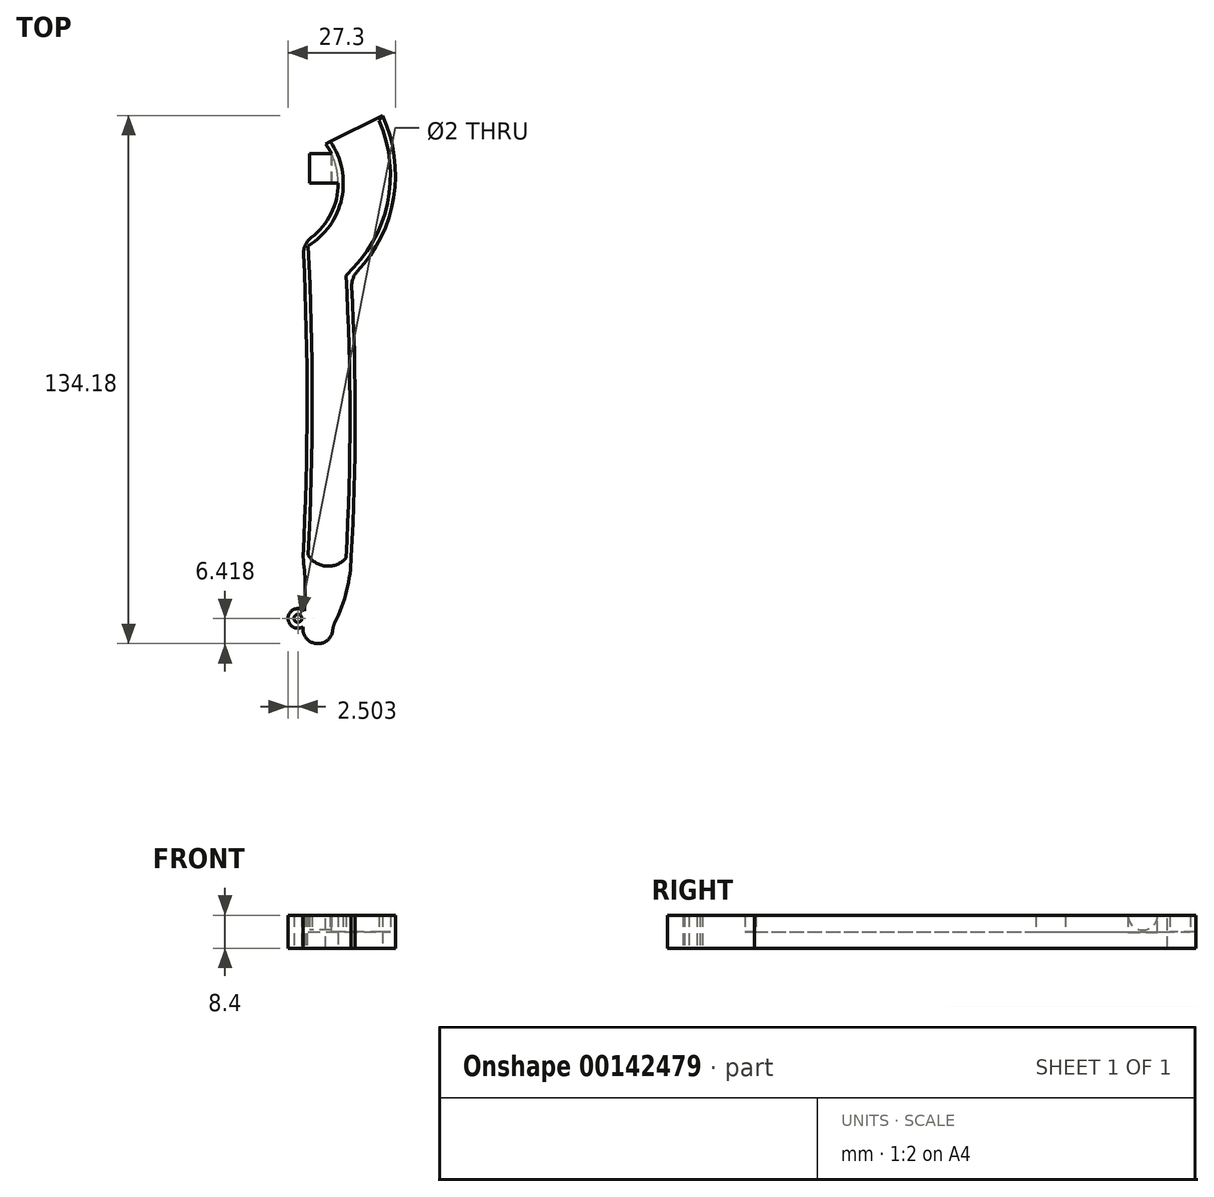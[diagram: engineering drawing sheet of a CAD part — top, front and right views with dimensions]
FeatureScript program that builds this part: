
annotation { "Feature Type Name" : "Feature", "Feature Type Description" : "" }
export const myFeature = defineFeature(function(context is Context, id is Id, definition is map)
    precondition{}
    {
        {
            var Q0;
            Q0=qCreatedBy(makeId("Top.planeOp"),FACE);
            var sketch = newSketch(context, id + "F0", { "sketchPlane" : qUnion([Q0])});
            skArc(sketch, "E0", {"start": v(-18, -31.8) * mm, "mid": v(-9.08, -15.9) * mm, "end": v(-18, 0) * mm});
            skArc(sketch, "E1", {"start": v(-8.38, -39.3) * mm, "mid": v(2.12, -21) * mm, "end": v(0, 0) * mm});
            skArc(sketch, "E2", {"start": v(-18, -110.4) * mm, "mid": v(-17, -71.1) * mm, "end": v(-18, -31.8) * mm});
            skArc(sketch, "E3", {"start": v(-8.38, -111.1) * mm, "mid": v(-7.37, -75.2) * mm, "end": v(-8.38, -39.3) * mm});
            skArc(sketch, "E4", {"start": v(-18, -110.4) * mm, "mid": v(-13.37, -113.18) * mm, "end": v(-8.38, -111.1) * mm});
            skLineSegment(sketch, "E5", {"start": v(0, 0) * mm, "end": v(-18, 0) * mm});
            skArc(sketch, "E6.0", {"start": v(-19.32, -110.8) * mm, "mid": v(-18.3, -70.94) * mm, "end": v(-19.34, -31.07) * mm});
            skLineSegment(sketch, "E6.1", {"start": v(0.84, 1.3) * mm, "end": v(-25.59, 1.3) * mm});
            skArc(sketch, "E6.2", {"start": v(-7.05, -39.84) * mm, "mid": v(3.54, -20.54) * mm, "end": v(0.84, 1.3) * mm});
            skArc(sketch, "E6.3", {"start": v(-19.34, -31.07) * mm, "mid": v(-10.7, -12.62) * mm, "end": v(-25.59, 1.3) * mm});
            skArc(sketch, "E6.4", {"start": v(-7.06, -110.8) * mm, "mid": v(-6.07, -75.32) * mm, "end": v(-7.05, -39.84) * mm});
            skArc(sketch, "E7", {"start": v(-19.32, -128.6) * mm, "mid": v(-18.75, -119.7) * mm, "end": v(-19.32, -110.8) * mm});
            skArc(sketch, "E8", {"start": v(-11.78, -128.6) * mm, "mid": v(-8.38, -119.98) * mm, "end": v(-7.06, -110.8) * mm});
            skArc(sketch, "E9", {"start": v(-19.32, -128.6) * mm, "mid": v(-15.55, -132.88) * mm, "end": v(-11.78, -128.6) * mm});
            skArc(sketch, "E10", {"start": v(-18.93, -124.62) * mm, "mid": v(-23.1, -126.21) * mm, "end": v(-19.32, -128.6) * mm});
            skCircle(sketch, "E11", {"center": v(-20.62, -126.46) * mm, "radius": 1 * mm});
            skLineSegment(sketch, "E12", {"start": v(-10.38, -15.9) * mm, "end": v(-17.68, -15.9) * mm});
            skLineSegment(sketch, "E13", {"start": v(-17.68, -15.9) * mm, "end": v(-17.68, -8.4) * mm});
            skLineSegment(sketch, "E14", {"start": v(-17.68, -8.4) * mm, "end": v(-12.09, -8.4) * mm});
            skSolve(sketch);
        }
        {
            var Q0;
            Q0=makeQuery(id+"F0.imprint","IMPRINT",FACE,{"disambiguationData":[TD([[makeQuery(id+"F0.imprint","IMPRINT",EDGE,{"derivedFrom":sQuery(id+"F0.wireOp",EDGE,"E0")}),1.0]])]});
            var Q1;
            {var subQ0=sQuery(id+"F0.wireOp",EDGE,"E10");Q1=makeQuery(id+"F0.imprint","IMPRINT",FACE,{"disambiguationData":[TD([[makeQuery(id+"F0.imprint","IMPRINT",EDGE,{"derivedFrom":subQ0}),1.0]])]});}
            extrude(context, id + "F1", {"entities" : qUnion([Q0, Q1]), "depth" : 8.4 * mm});
        }
        {
            var Q0;
            Q0=makeQuery(id+"F0.imprint","IMPRINT",FACE,{"disambiguationData":[TD([[makeQuery(id+"F0.imprint","IMPRINT",EDGE,{"derivedFrom":sQuery(id+"F0.wireOp",EDGE,"E0")}),-1.0]])]});
            extrude(context, id + "F2", {"entities" : qUnion([Q0]), "operationType" : NewBodyOperationType.ADD, "depth" : 4.2 * mm});
        }
        {
            var Q0;
            {var subQ0=sQuery(id+"F0.wireOp",EDGE,"E12");Q0=makeQuery(id+"F0.imprint","IMPRINT",FACE,{"disambiguationData":[TD([[makeQuery(id+"F0.imprint","IMPRINT",EDGE,{"derivedFrom":subQ0}),-1.0]])]});}
            extrude(context, id + "F3", {"entities" : qUnion([Q0]), "operationType" : NewBodyOperationType.ADD, "depth" : 8.4 * mm});
        }
        {
            var Q0;
            {var subQ0=sQuery(id+"F0.wireOp",EDGE,"E12");Q0=makeQuery(id+"F0.imprint","IMPRINT",FACE,{"disambiguationData":[TD([[makeQuery(id+"F0.imprint","IMPRINT",EDGE,{"derivedFrom":subQ0}),-1.0]])]});}
            extrude(context, id + "F4", {"entities" : qUnion([Q0]), "operationType" : NewBodyOperationType.REMOVE, "depth" : 4 * mm});
        }
        {
            var Q0;
            Q0=makeQuery(id+"F3.opExtrude","SWEPT_FACE",FACE,{"disambiguationData":[OSD([sQuery(id+"F0.wireOp",EDGE,"E13")])]});
            var sketch = newSketch(context, id + "F5", { "sketchPlane" : qUnion([Q0])});
            skLineSegment(sketch, "E15.0", {"start": v(8.4, 8.4) * mm, "end": v(8.4, 4) * mm});
            skLineSegment(sketch, "E15.1", {"start": v(15.9, 8.4) * mm, "end": v(8.4, 8.4) * mm});
            skLineSegment(sketch, "E15.2", {"start": v(15.9, 8.4) * mm, "end": v(15.9, 4) * mm});
            skLineSegment(sketch, "E15.3", {"start": v(15.9, 4) * mm, "end": v(8.4, 4) * mm});
            skSolve(sketch);
        }
        {
            var Q0;
            {var subQ0=sQuery(id+"F0.wireOp",EDGE,"E6.3");Q0=makeQuery(id+"F3.boolean.opBoolean","MERGE",FACE,{"derivedFrom":[makeQuery(id+"F1.opExtrude","CAP_FACE",FACE,{"disambiguationData":[OSD([sQuery(id+"F0.wireOp",EDGE,"E0"),sQuery(id+"F0.wireOp",EDGE,"E1"),sQuery(id+"F0.wireOp",EDGE,"E2"),sQuery(id+"F0.wireOp",EDGE,"E3"),sQuery(id+"F0.wireOp",EDGE,"E4"),sQuery(id+"F0.wireOp",EDGE,"E5"),sQuery(id+"F0.wireOp",EDGE,"E6.0"),sQuery(id+"F0.wireOp",EDGE,"E6.1"),sQuery(id+"F0.wireOp",EDGE,"E6.2"),subQ0,sQuery(id+"F0.wireOp",EDGE,"E6.4"),sQuery(id+"F0.wireOp",EDGE,"E7"),sQuery(id+"F0.wireOp",EDGE,"E8"),sQuery(id+"F0.wireOp",EDGE,"E9"),sQuery(id+"F0.wireOp",EDGE,"E10"),sQuery(id+"F0.wireOp",EDGE,"E11")])],"isStart":false}),makeQuery(id+"F3.opExtrude","CAP_FACE",FACE,{"disambiguationData":[OSD([subQ0,sQuery(id+"F0.wireOp",EDGE,"E12"),sQuery(id+"F0.wireOp",EDGE,"E13"),sQuery(id+"F0.wireOp",EDGE,"E14")])],"isStart":false})]});}
            var sketch = newSketch(context, id + "F6", { "sketchPlane" : qUnion([Q0])});
            skLineSegment(sketch, "E16.0", {"start": v(0.84, 1.3) * mm, "end": v(-25.59, 1.3) * mm});
            skArc(sketch, "E16.1", {"start": v(-7.05, -39.84) * mm, "mid": v(3.54, -20.54) * mm, "end": v(0.84, 1.3) * mm});
            skArc(sketch, "E16.2", {"start": v(-12.09, -8.4) * mm, "mid": v(-17.6, -1.83) * mm, "end": v(-25.59, 1.3) * mm});
            skLineSegment(sketch, "E16.3", {"start": v(-17.68, -8.4) * mm, "end": v(-12.09, -8.4) * mm});
            skLineSegment(sketch, "E17", {"start": v(0.84, 1.3) * mm, "end": v(-13.56, -5.9) * mm});
            skSolve(sketch);
        }
        {
            var Q0;
            {var subQ1=sQuery(id+"F6.wireOp",EDGE,"E16.0");Q0=makeQuery(id+"F6.imprint","IMPRINT",FACE,{"disambiguationData":[TD([[makeQuery(id+"F6.imprint","IMPRINT",EDGE,{"derivedFrom":subQ1}),1.0]])]});}
            var Q1;
            {var subQ0=sQuery(id+"F6.wireOp",EDGE,"E17");var subQ1=makeQuery(id+"F1.opExtrude","CAP_EDGE",EDGE,{"disambiguationData":[OSD([sQuery(id+"F0.wireOp",EDGE,"E5")])],"isStart":false});var subQ2=makeQuery(id+"F6.imprint","INTERSECT",VERTEX,{"derivedFrom":[subQ1,subQ0]});Q1=makeQuery(id+"F6.imprint","IMPRINT",FACE,{"disambiguationData":[TD([[makeQuery(id+"F6.imprint","IMPRINT",EDGE,{"disambiguationData":[TD([[subQ2,-1.0]])],"derivedFrom":subQ0}),-1.0]])]});}
            extrude(context, id + "F7", {"entities" : qUnion([Q0, Q1]), "operationType" : NewBodyOperationType.REMOVE, "oppositeDirection" : true, "depth" : 25 * mm});
        }
        {
            var Q0;
            {var subQ0=sQuery(id+"F0.wireOp",EDGE,"E6.3");Q0=makeQuery(id+"F3.boolean.opBoolean","MERGE",FACE,{"derivedFrom":[makeQuery(id+"F1.opExtrude","CAP_FACE",FACE,{"disambiguationData":[OSD([sQuery(id+"F0.wireOp",EDGE,"E0"),sQuery(id+"F0.wireOp",EDGE,"E1"),sQuery(id+"F0.wireOp",EDGE,"E2"),sQuery(id+"F0.wireOp",EDGE,"E3"),sQuery(id+"F0.wireOp",EDGE,"E4"),sQuery(id+"F0.wireOp",EDGE,"E5"),sQuery(id+"F0.wireOp",EDGE,"E6.0"),sQuery(id+"F0.wireOp",EDGE,"E6.1"),sQuery(id+"F0.wireOp",EDGE,"E6.2"),subQ0,sQuery(id+"F0.wireOp",EDGE,"E6.4"),sQuery(id+"F0.wireOp",EDGE,"E7"),sQuery(id+"F0.wireOp",EDGE,"E8"),sQuery(id+"F0.wireOp",EDGE,"E9"),sQuery(id+"F0.wireOp",EDGE,"E10"),sQuery(id+"F0.wireOp",EDGE,"E11")])],"isStart":false}),makeQuery(id+"F3.opExtrude","CAP_FACE",FACE,{"disambiguationData":[OSD([subQ0,sQuery(id+"F0.wireOp",EDGE,"E12"),sQuery(id+"F0.wireOp",EDGE,"E13"),sQuery(id+"F0.wireOp",EDGE,"E14")])],"isStart":false})]});}
            var sketch = newSketch(context, id + "F8", { "sketchPlane" : qUnion([Q0])});
            skArc(sketch, "E18.0", {"start": v(-7.05, -39.84) * mm, "mid": v(3.54, -20.54) * mm, "end": v(0.84, 1.3) * mm});
            skLineSegment(sketch, "E18.1", {"start": v(0.84, 1.3) * mm, "end": v(-1.76, 0) * mm});
            skLineSegment(sketch, "E18.2", {"start": v(0, 0) * mm, "end": v(-1.76, 0) * mm});
            skArc(sketch, "E18.3", {"start": v(-8.38, -39.3) * mm, "mid": v(2.12, -21) * mm, "end": v(0, 0) * mm});
            skLineSegment(sketch, "E19", {"start": v(0.84, 1.3) * mm, "end": v(0, 0) * mm});
            skSolve(sketch);
        }
        {
            var Q0;
            Q0=makeQuery(id+"F8.imprint","IMPRINT",FACE,{"disambiguationData":[TD([[makeQuery(id+"F8.imprint","IMPRINT",EDGE,{"derivedFrom":sQuery(id+"F8.wireOp",EDGE,"E18.1")}),1.0]])]});
            extrude(context, id + "F9", {"entities" : qUnion([Q0]), "operationType" : NewBodyOperationType.REMOVE, "oppositeDirection" : true, "depth" : 4.2 * mm});
        }
        {
            var Q0;
            Q0=makeQuery(id+"F5.imprint","IMPRINT",FACE,{"disambiguationData":[TD([[makeQuery(id+"F5.imprint","IMPRINT",EDGE,{"derivedFrom":sQuery(id+"F5.wireOp",EDGE,"E15.0")}),1.0]])]});
            var sketch = newSketch(context, id + "F10", { "sketchPlane" : qUnion([Q0])});
            skLineSegment(sketch, "E20.0", {"start": v(15.9, 8.4) * mm, "end": v(8.4, 8.4) * mm});
            skLineSegment(sketch, "E20.1", {"start": v(8.4, 8.4) * mm, "end": v(8.4, 4) * mm});
            skLineSegment(sketch, "E20.2", {"start": v(15.9, 4) * mm, "end": v(8.4, 4) * mm});
            skLineSegment(sketch, "E20.3", {"start": v(15.9, 8.4) * mm, "end": v(15.9, 4) * mm});
            skArc(sketch, "E21", {"start": v(8.4, 8.4) * mm, "mid": v(12.15, 4.65) * mm, "end": v(15.9, 8.4) * mm});
            skSolve(sketch);
        }
        {
            var Q0;
            Q0=makeQuery(id+"F10.imprint","IMPRINT",FACE,{"disambiguationData":[TD([[makeQuery(id+"F10.imprint","IMPRINT",EDGE,{"derivedFrom":sQuery(id+"F10.wireOp",EDGE,"E20.2")}),-1.0]])]});
            extrude(context, id + "F11", {"entities" : qUnion([Q0]), "operationType" : NewBodyOperationType.REMOVE, "oppositeDirection" : true, "depth" : 5.6 * mm});
        }
        {
            var Q0;
            Q0=makeQuery(id+"F1.opExtrude","SWEPT_EDGE",EDGE,{"disambiguationData":[OSD([sQuery(id+"F0.wireOp",EDGE,"E6.0"),sQuery(id+"F0.wireOp",EDGE,"E6.3")])]});
            var Q1;
            Q1=makeQuery(id+"F1.opExtrude","SWEPT_EDGE",EDGE,{"disambiguationData":[OSD([sQuery(id+"F0.wireOp",EDGE,"E6.2"),sQuery(id+"F0.wireOp",EDGE,"E6.4")])]});
            var Q2;
            Q2=makeQuery(id+"F1.opExtrude","SWEPT_EDGE",EDGE,{"disambiguationData":[OSD([sQuery(id+"F0.wireOp",EDGE,"E8"),sQuery(id+"F0.wireOp",EDGE,"E9")])]});
            fillet(context, id + "F12", {"entities" : qUnion([Q0, Q1, Q2]), "radius" : 5 * mm, "tangentPropagation" : true, "allowEdgeOverflow" : false});
        }
    });
